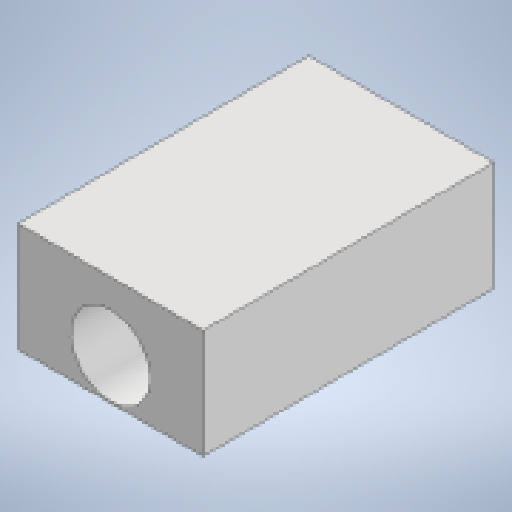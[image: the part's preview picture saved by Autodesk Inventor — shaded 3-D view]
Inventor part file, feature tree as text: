
AUTODESK INVENTOR PART (.ipt)
format: ipt  version: 2023 (Build 270158000, 158)  size: 180,224 bytes
history: native  units: mm
features: other x3, extrude x2, sketch x2, reference x1
ambient origin geometry x8: Origin, YZ Plane, XZ Plane, XY Plane, X Axis, Y Axis, Z Axis, Center Point
bodies: Body1 (feature_tree)
feature tree (8):
  other  "Bryła1"
  extrude  "Wyciągnięcie proste1"  Depth=14.0mm
  extrude  "Wyciągnięcie proste2"  Depth=22.0mm
  sketch  "Szkic1"
  sketch  "Szkic2"
  reference  "Odniesienie1"
  other  "Zespół2"
  other  "silnik_2:1"
